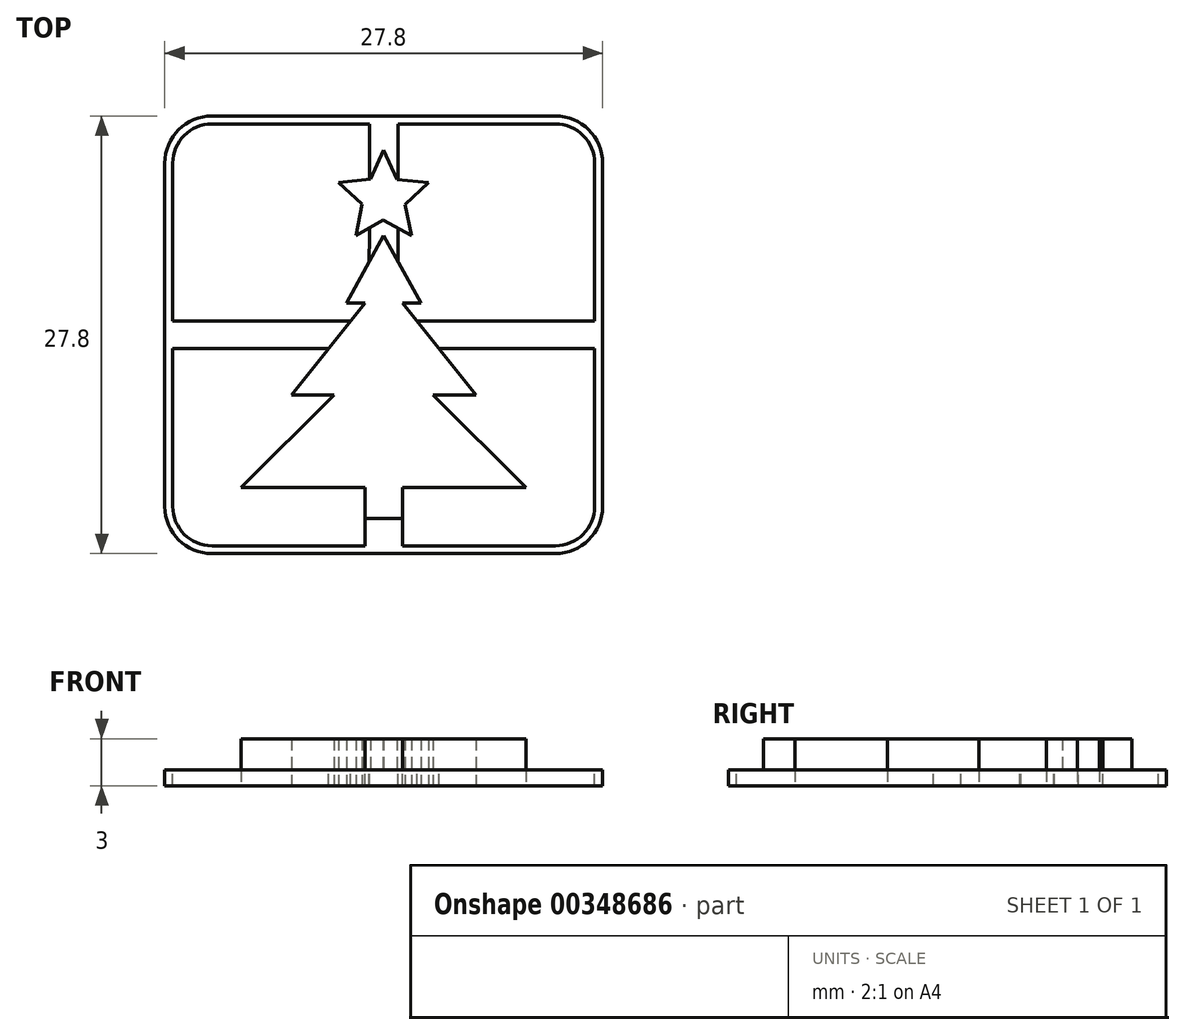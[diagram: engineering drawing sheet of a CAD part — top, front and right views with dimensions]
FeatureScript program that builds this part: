
annotation { "Feature Type Name" : "Feature", "Feature Type Description" : "" }
export const myFeature = defineFeature(function(context is Context, id is Id, definition is map)
    precondition{}
    {
        {
            var Q0;
            Q0=qCreatedBy(makeId("Top.planeOp"),FACE);
            var sketch = newSketch(context, id + "F0", { "sketchPlane" : qUnion([Q0])});
            skLineSegment(sketch, "E0", {"start": v(-13.9, 10.9) * mm, "end": v(-13.9, -10.9) * mm});
            skLineSegment(sketch, "E1", {"start": v(13.9, -10.9) * mm, "end": v(13.9, 10.9) * mm});
            skLineSegment(sketch, "E2", {"start": v(-10.9, 13.9) * mm, "end": v(10.9, 13.9) * mm});
            skLineSegment(sketch, "E3", {"start": v(-10.9, -13.9) * mm, "end": v(10.9, -13.9) * mm});
            skLineSegment(sketch, "E4", {"start": v(0, 13.9) * mm, "end": v(0, -13.9) * mm, "construction": true});
            skLineSegment(sketch, "E5", {"start": v(-13.9, 0) * mm, "end": v(13.9, 0) * mm, "construction": true});
            skPoint(sketch, "E6", {"position": v(0, 0) * mm});
            skPoint(sketch, "E7", {"position": v(0, 13.9) * mm});
            skPoint(sketch, "E8", {"position": v(0, -13.9) * mm});
            skPoint(sketch, "E9", {"position": v(-13.9, 0) * mm});
            skPoint(sketch, "E10", {"position": v(13.9, 0) * mm});
            skArc(sketch, "E11", {"start": v(-10.9, 13.9) * mm, "mid": v(-13.02, 13.02) * mm, "end": v(-13.9, 10.9) * mm});
            skArc(sketch, "E12", {"start": v(13.9, 10.9) * mm, "mid": v(13.02, 13.02) * mm, "end": v(10.9, 13.9) * mm});
            skArc(sketch, "E13", {"start": v(-13.9, -10.9) * mm, "mid": v(-13.02, -13.02) * mm, "end": v(-10.9, -13.9) * mm});
            skArc(sketch, "E14", {"start": v(10.9, -13.9) * mm, "mid": v(13.02, -13.02) * mm, "end": v(13.9, -10.9) * mm});
            skSolve(sketch);
        }
        {
            var Q0;
            Q0=makeQuery(id+"F0.imprint","IMPRINT",FACE,{"disambiguationData":[TD([[makeQuery(id+"F0.imprint","IMPRINT",EDGE,{"derivedFrom":sQuery(id+"F0.wireOp",EDGE,"E0")}),1.0]])]});
            extrude(context, id + "F1", {"entities" : qUnion([Q0]), "depth" : 1 * mm});
        }
        {
            var Q0;
            Q0=makeQuery(id+"F1.opExtrude","CAP_FACE",FACE,{"disambiguationData":[OSD([sQuery(id+"F0.wireOp",EDGE,"E0"),sQuery(id+"F0.wireOp",EDGE,"E1"),sQuery(id+"F0.wireOp",EDGE,"E2"),sQuery(id+"F0.wireOp",EDGE,"E3"),sQuery(id+"F0.wireOp",EDGE,"E11"),sQuery(id+"F0.wireOp",EDGE,"E12"),sQuery(id+"F0.wireOp",EDGE,"E13"),sQuery(id+"F0.wireOp",EDGE,"E14")])],"isStart":false});
            var sketch = newSketch(context, id + "F2", { "sketchPlane" : qUnion([Q0])});
            skLineSegment(sketch, "E15", {"start": v(-13.4, 10.9) * mm, "end": v(-13.4, -10.9) * mm});
            skLineSegment(sketch, "E16", {"start": v(-10.9, -13.4) * mm, "end": v(10.9, -13.4) * mm});
            skLineSegment(sketch, "E17", {"start": v(13.4, -10.9) * mm, "end": v(13.4, 10.9) * mm});
            skLineSegment(sketch, "E18", {"start": v(-10.9, 13.4) * mm, "end": v(10.9, 13.4) * mm});
            skLineSegment(sketch, "E19", {"start": v(0, 13.4) * mm, "end": v(0, -13.4) * mm, "construction": true});
            skLineSegment(sketch, "E20", {"start": v(-13.4, 0) * mm, "end": v(13.4, 0) * mm, "construction": true});
            skArc(sketch, "E21", {"start": v(13.4, 10.9) * mm, "mid": v(12.67, 12.67) * mm, "end": v(10.9, 13.4) * mm});
            skArc(sketch, "E22", {"start": v(10.9, -13.4) * mm, "mid": v(12.67, -12.67) * mm, "end": v(13.4, -10.9) * mm});
            skArc(sketch, "E23", {"start": v(-13.4, -10.9) * mm, "mid": v(-12.67, -12.67) * mm, "end": v(-10.9, -13.4) * mm});
            skLineSegment(sketch, "E24", {"start": v(-1.2, -11.68) * mm, "end": v(-1.2, -9.68) * mm});
            skLineSegment(sketch, "E25", {"start": v(-1.2, -9.68) * mm, "end": v(-9.04, -9.68) * mm});
            skLineSegment(sketch, "E26", {"start": v(-9.04, -9.68) * mm, "end": v(-3.15, -3.8) * mm});
            skLineSegment(sketch, "E27", {"start": v(-3.15, -3.8) * mm, "end": v(-5.86, -3.8) * mm});
            skLineSegment(sketch, "E28", {"start": v(-5.86, -3.8) * mm, "end": v(-1.2, 2.02) * mm});
            skLineSegment(sketch, "E29", {"start": v(-1.2, 2.02) * mm, "end": v(-2.37, 2.02) * mm});
            skLineSegment(sketch, "E30", {"start": v(-2.37, 2.02) * mm, "end": v(0, 6.3) * mm});
            skLineSegment(sketch, "E31", {"start": v(-1.2, -11.68) * mm, "end": v(0, -11.68) * mm});
            skLineSegment(sketch, "E32.MirrorCS", {"start": v(1.2, -11.68) * mm, "end": v(0, -11.68) * mm});
            skLineSegment(sketch, "E33.MirrorCS", {"start": v(1.2, -11.68) * mm, "end": v(1.2, -9.68) * mm});
            skLineSegment(sketch, "E34.MirrorCS", {"start": v(1.2, -9.68) * mm, "end": v(9.04, -9.68) * mm});
            skLineSegment(sketch, "E35.MirrorCS", {"start": v(2.37, 2.02) * mm, "end": v(0, 6.3) * mm});
            skLineSegment(sketch, "E36.MirrorCS", {"start": v(1.2, 2.02) * mm, "end": v(2.37, 2.02) * mm});
            skLineSegment(sketch, "E37.MirrorCS", {"start": v(3.15, -3.8) * mm, "end": v(5.86, -3.8) * mm});
            skLineSegment(sketch, "E38.MirrorCS", {"start": v(5.86, -3.8) * mm, "end": v(1.2, 2.02) * mm});
            skLineSegment(sketch, "E39.MirrorCS", {"start": v(9.04, -9.68) * mm, "end": v(3.15, -3.8) * mm});
            skCircle(sketch, "E40.cCircle", {"center": v(0, 8.73) * mm, "radius": 2.44 * mm, "construction": true});
            skLineSegment(sketch, "E40.0", {"start": v(0, 11.74) * mm, "end": v(2.86, 9.66) * mm, "construction": true});
            skLineSegment(sketch, "E40.1", {"start": v(2.86, 9.66) * mm, "end": v(1.77, 6.3) * mm, "construction": true});
            skLineSegment(sketch, "E40.2", {"start": v(1.77, 6.3) * mm, "end": v(-1.77, 6.3) * mm, "construction": true});
            skLineSegment(sketch, "E40.3", {"start": v(-1.77, 6.3) * mm, "end": v(-2.86, 9.66) * mm, "construction": true});
            skLineSegment(sketch, "E40.4", {"start": v(-2.86, 9.66) * mm, "end": v(0, 11.74) * mm, "construction": true});
            skPoint(sketch, "E40.0.midPoint", {"position": v(1.43, 10.7) * mm});
            skPoint(sketch, "E41", {"position": v(0, 0) * mm});
            skCircle(sketch, "E42.cCircle", {"center": v(0, 8.73) * mm, "radius": 1.16 * mm, "construction": true});
            skLineSegment(sketch, "E42.0", {"start": v(0.86, 9.87) * mm, "end": v(1.36, 8.26) * mm, "construction": true});
            skLineSegment(sketch, "E42.1", {"start": v(1.36, 8.26) * mm, "end": v(-0.03, 7.3) * mm, "construction": true});
            skLineSegment(sketch, "E42.2", {"start": v(-0.03, 7.3) * mm, "end": v(-1.37, 8.3) * mm, "construction": true});
            skLineSegment(sketch, "E42.3", {"start": v(-1.37, 8.3) * mm, "end": v(-0.82, 9.9) * mm, "construction": true});
            skLineSegment(sketch, "E42.4", {"start": v(-0.82, 9.9) * mm, "end": v(0.86, 9.87) * mm, "construction": true});
            skPoint(sketch, "E42.0.midPoint", {"position": v(1.1, 9.07) * mm});
            skLineSegment(sketch, "E43", {"start": v(-0.82, 9.9) * mm, "end": v(-2.86, 9.66) * mm});
            skLineSegment(sketch, "E44", {"start": v(-1.37, 8.3) * mm, "end": v(-2.86, 9.66) * mm});
            skLineSegment(sketch, "E45", {"start": v(-1.37, 8.3) * mm, "end": v(-1.77, 6.3) * mm});
            skLineSegment(sketch, "E46", {"start": v(-0.03, 7.3) * mm, "end": v(-1.77, 6.3) * mm});
            skLineSegment(sketch, "E47", {"start": v(-0.03, 7.3) * mm, "end": v(1.77, 6.3) * mm});
            skLineSegment(sketch, "E48", {"start": v(1.77, 6.3) * mm, "end": v(1.36, 8.26) * mm});
            skLineSegment(sketch, "E49", {"start": v(1.36, 8.26) * mm, "end": v(2.86, 9.66) * mm});
            skLineSegment(sketch, "E50", {"start": v(2.86, 9.66) * mm, "end": v(0.86, 9.87) * mm});
            skLineSegment(sketch, "E51", {"start": v(0.86, 9.87) * mm, "end": v(0, 11.74) * mm});
            skLineSegment(sketch, "E52", {"start": v(0, 11.74) * mm, "end": v(-0.82, 9.9) * mm});
            skArc(sketch, "E53.MirrorCS", {"start": v(10.9, 13.4) * mm, "mid": v(12.67, 12.67) * mm, "end": v(13.4, 10.9) * mm});
            skArc(sketch, "E54", {"start": v(-10.9, 13.4) * mm, "mid": v(-12.67, 12.67) * mm, "end": v(-13.4, 10.9) * mm});
            skLineSegment(sketch, "E55", {"start": v(-13.4, 0.87) * mm, "end": v(13.4, 0.87) * mm});
            skLineSegment(sketch, "E56", {"start": v(13.4, 0.87) * mm, "end": v(13.4, -0.87) * mm});
            skLineSegment(sketch, "E57", {"start": v(13.4, -0.87) * mm, "end": v(-13.4, -0.87) * mm});
            skLineSegment(sketch, "E58", {"start": v(-1.2, -11.68) * mm, "end": v(-1.2, -13.4) * mm});
            skLineSegment(sketch, "E59", {"start": v(1.2, -11.68) * mm, "end": v(1.2, -13.4) * mm});
            skLineSegment(sketch, "E60", {"start": v(-0.9, 13.4) * mm, "end": v(-0.9, 9.9) * mm});
            skLineSegment(sketch, "E61", {"start": v(0.9, 13.4) * mm, "end": v(0.9, 9.87) * mm});
            skLineSegment(sketch, "E62", {"start": v(-0.9, 6.3) * mm, "end": v(-0.93, 4.6) * mm});
            skLineSegment(sketch, "E63", {"start": v(0.9, 6.3) * mm, "end": v(0.9, 4.66) * mm});
            skLineSegment(sketch, "E64", {"start": v(-0.9, 6.3) * mm, "end": v(-0.9, 6.79) * mm});
            skLineSegment(sketch, "E65", {"start": v(0.9, 6.3) * mm, "end": v(0.9, 6.77) * mm});
            skSolve(sketch);
        }
        {
            var Q0;
            {var subQ0=sQuery(id+"F2.wireOp",EDGE,"c0bee297-e610-4342-9203-62b1a1aad97730.MirrorCS");Q0=makeQuery(id+"F2.imprint","IMPRINT",FACE,{"disambiguationData":[TD([[makeQuery(id+"F2.imprint","IMPRINT",EDGE,{"derivedFrom":subQ0}),-1.0]])]});}
            var Q1;
            {var subQ0=sQuery(id+"F2.wireOp",EDGE,"c0bee297-e610-4342-9203-62b1a1aad97742.MirrorCS");Q1=makeQuery(id+"F2.imprint","IMPRINT",FACE,{"disambiguationData":[TD([[makeQuery(id+"F2.imprint","IMPRINT",EDGE,{"derivedFrom":subQ0}),1.0]])]});}
            var Q2;
            Q2=makeQuery(id+"F2.imprint","IMPRINT",FACE,{"disambiguationData":[TD([[makeQuery(id+"F2.imprint","IMPRINT",EDGE,{"derivedFrom":sQuery(id+"F2.wireOp",EDGE,"E43")}),1.0]])]});
            var Q3;
            {var subQ0=sQuery(id+"F2.wireOp",EDGE,"E35.MirrorCS");var subQ1=sQuery(id+"F2.wireOp",EDGE,"E30");var subQ2=makeQuery(id+"F2.imprint","INTERSECT",VERTEX,{"derivedFrom":[subQ1,subQ0]});Q3=makeQuery(id+"F2.imprint","IMPRINT",FACE,{"disambiguationData":[TD([[makeQuery(id+"F2.imprint","IMPRINT",EDGE,{"disambiguationData":[TD([[subQ2,1.0]])],"derivedFrom":subQ1}),-1.0]])]});}
            var Q4;
            {var subQ5=sQuery(id+"F2.wireOp",EDGE,"E29");Q4=makeQuery(id+"F2.imprint","IMPRINT",FACE,{"disambiguationData":[TD([[makeQuery(id+"F2.imprint","IMPRINT",EDGE,{"derivedFrom":subQ5}),-1.0]])]});}
            var Q5;
            Q5=makeQuery(id+"F2.imprint","IMPRINT",FACE,{"disambiguationData":[TD([[makeQuery(id+"F2.imprint","IMPRINT",EDGE,{"derivedFrom":sQuery(id+"F2.wireOp",EDGE,"E24")}),-1.0]])]});
            var Q6;
            {var subQ0=sQuery(id+"F2.wireOp",EDGE,"E57");var subQ1=sQuery(id+"F2.wireOp",EDGE,"E28");var subQ2=makeQuery(id+"F2.imprint","INTERSECT",VERTEX,{"derivedFrom":[subQ1,subQ0]});Q6=makeQuery(id+"F2.imprint","IMPRINT",FACE,{"disambiguationData":[TD([[makeQuery(id+"F2.imprint","IMPRINT",EDGE,{"disambiguationData":[TD([[subQ2,-1.0]])],"derivedFrom":subQ1}),-1.0]])]});}
            extrude(context, id + "F3", {"entities" : qUnion([Q0, Q1, Q2, Q3, Q4, Q5, Q6]), "operationType" : NewBodyOperationType.ADD, "depth" : 2 * mm});
        }
        {
            var Q0;
            {var subQ8=sQuery(id+"F2.wireOp",EDGE,"E29");Q0=makeQuery(id+"F2.imprint","IMPRINT",FACE,{"disambiguationData":[TD([[makeQuery(id+"F2.imprint","IMPRINT",EDGE,{"derivedFrom":subQ8}),1.0]])]});}
            var Q1;
            {var subQ7=sQuery(id+"F2.wireOp",EDGE,"E36.MirrorCS");Q1=makeQuery(id+"F2.imprint","IMPRINT",FACE,{"disambiguationData":[TD([[makeQuery(id+"F2.imprint","IMPRINT",EDGE,{"derivedFrom":subQ7}),-1.0]])]});}
            var Q2;
            {var subQ0=sQuery(id+"F2.wireOp",EDGE,"E23");Q2=makeQuery(id+"F2.imprint","IMPRINT",FACE,{"disambiguationData":[TD([[makeQuery(id+"F2.imprint","IMPRINT",EDGE,{"derivedFrom":subQ0}),1.0]])]});}
            var Q3;
            {var subQ0=sQuery(id+"F2.wireOp",EDGE,"E22");Q3=makeQuery(id+"F2.imprint","IMPRINT",FACE,{"disambiguationData":[TD([[makeQuery(id+"F2.imprint","IMPRINT",EDGE,{"derivedFrom":subQ0}),1.0]])]});}
            extrude(context, id + "F4", {"entities" : qUnion([Q0, Q1, Q2, Q3]), "operationType" : NewBodyOperationType.REMOVE, "oppositeDirection" : true, "depth" : 25 * mm});
        }
    });
